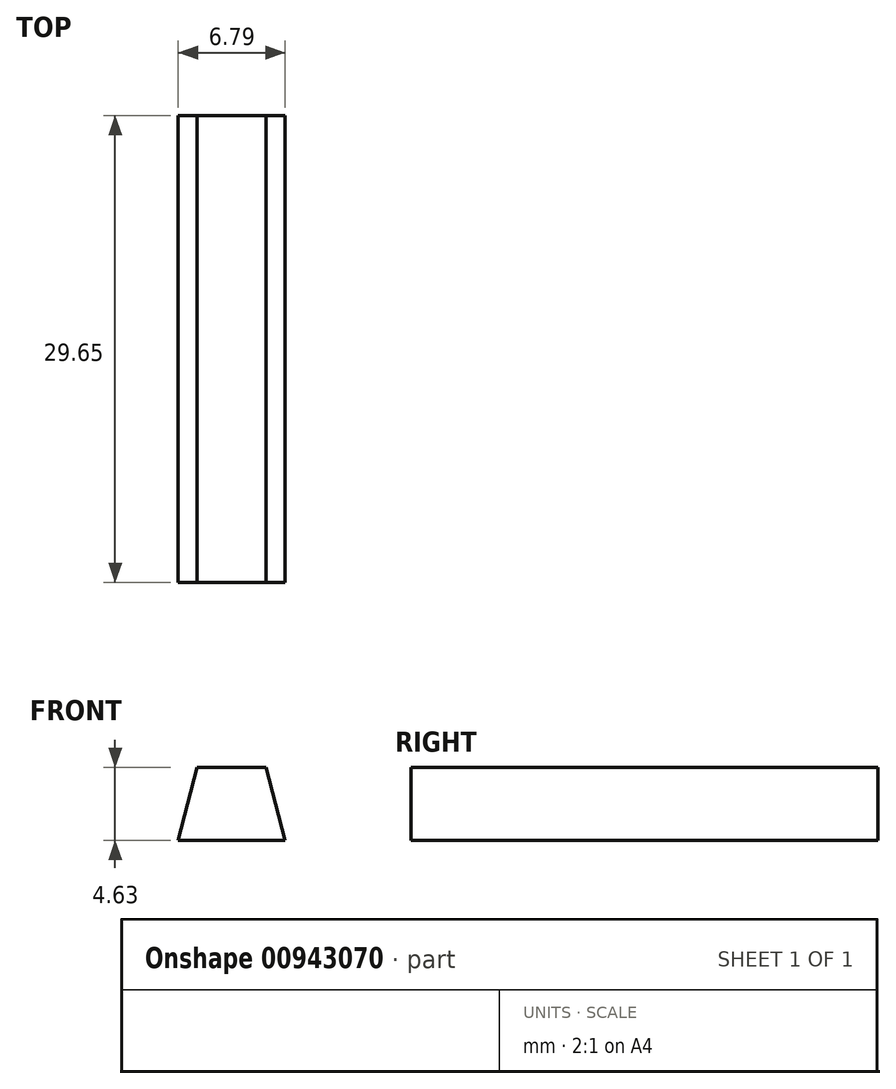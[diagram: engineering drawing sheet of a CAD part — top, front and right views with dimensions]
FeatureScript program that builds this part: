
annotation { "Feature Type Name" : "Feature", "Feature Type Description" : "" }
export const myFeature = defineFeature(function(context is Context, id is Id, definition is map)
    precondition{}
    {
        {
            var Q0;
            Q0=qCreatedBy(makeId("Top.planeOp"),FACE);
            var sketch = newSketch(context, id + "F0", { "sketchPlane" : qUnion([Q0])});
            skLineSegment(sketch, "E0.bottom", {"start": v(0, 0) * mm, "end": v(6.79, 0) * mm});
            skLineSegment(sketch, "E0.top", {"start": v(0, -29.65) * mm, "end": v(6.79, -29.65) * mm});
            skLineSegment(sketch, "E0.left", {"start": v(0, 0) * mm, "end": v(0, -29.65) * mm});
            skLineSegment(sketch, "E0.right", {"start": v(6.79, 0) * mm, "end": v(6.79, -29.65) * mm});
            skSolve(sketch);
        }
        {
            var Q0;
            Q0 = qSketchRegion(id + "F0", true);
            extrude(context, id + "F1", {"entities" : qUnion([Q0]), "depth" : 4.63 * mm, "offsetDistance" : 25.4 * mm});
        }
        {
            var Q0;
            Q0=makeQuery(id+"F1.opExtrude","SWEPT_FACE",FACE,{"disambiguationData":[OSD([sQuery(id+"F0.wireOp",EDGE,"E0.top")])]});
            var sketch = newSketch(context, id + "F2", { "sketchPlane" : qUnion([Q0])});
            skLineSegment(sketch, "E1", {"start": v(3.4, 0) * mm, "end": v(3.4, 13.03) * mm});
            skPoint(sketch, "E1.endSnap0", {"position": v(3.4, 4.63) * mm});
            skLineSegment(sketch, "E2", {"start": v(3.4, 13.03) * mm, "end": v(0, 0) * mm});
            skLineSegment(sketch, "E3", {"start": v(0, 0) * mm, "end": v(3.4, 13.03) * mm});
            skLineSegment(sketch, "E4", {"start": v(3.4, 13.03) * mm, "end": v(6.79, 0) * mm});
            skSolve(sketch);
        }
        {
            var Q0;
            {var subQ1=sQuery(id+"F0.wireOp",EDGE,"E0.top");var subQ2=makeQuery(id+"F1.opExtrude","SWEPT_EDGE",EDGE,{"disambiguationData":[OSD([subQ1,sQuery(id+"F0.wireOp",EDGE,"E0.right")])]});Q0=makeQuery(id+"F2.imprint","IMPRINT",FACE,{"disambiguationData":[TD([[makeQuery(id+"F2.imprint","IMPRINT",EDGE,{"derivedFrom":subQ2}),-1.0]])]});}
            var Q1;
            {var subQ1=sQuery(id+"F0.wireOp",EDGE,"E0.top");var subQ2=makeQuery(id+"F1.opExtrude","SWEPT_EDGE",EDGE,{"disambiguationData":[OSD([subQ1,sQuery(id+"F0.wireOp",EDGE,"E0.left")])]});Q1=makeQuery(id+"F2.imprint","IMPRINT",FACE,{"disambiguationData":[TD([[makeQuery(id+"F2.imprint","IMPRINT",EDGE,{"derivedFrom":subQ2}),1.0]])]});}
            extrude(context, id + "F3", {"entities" : qUnion([Q0, Q1]), "operationType" : NewBodyOperationType.REMOVE, "oppositeDirection" : true, "depth" : 38.27 * mm, "offsetDistance" : 25.4 * mm});
        }
    });
